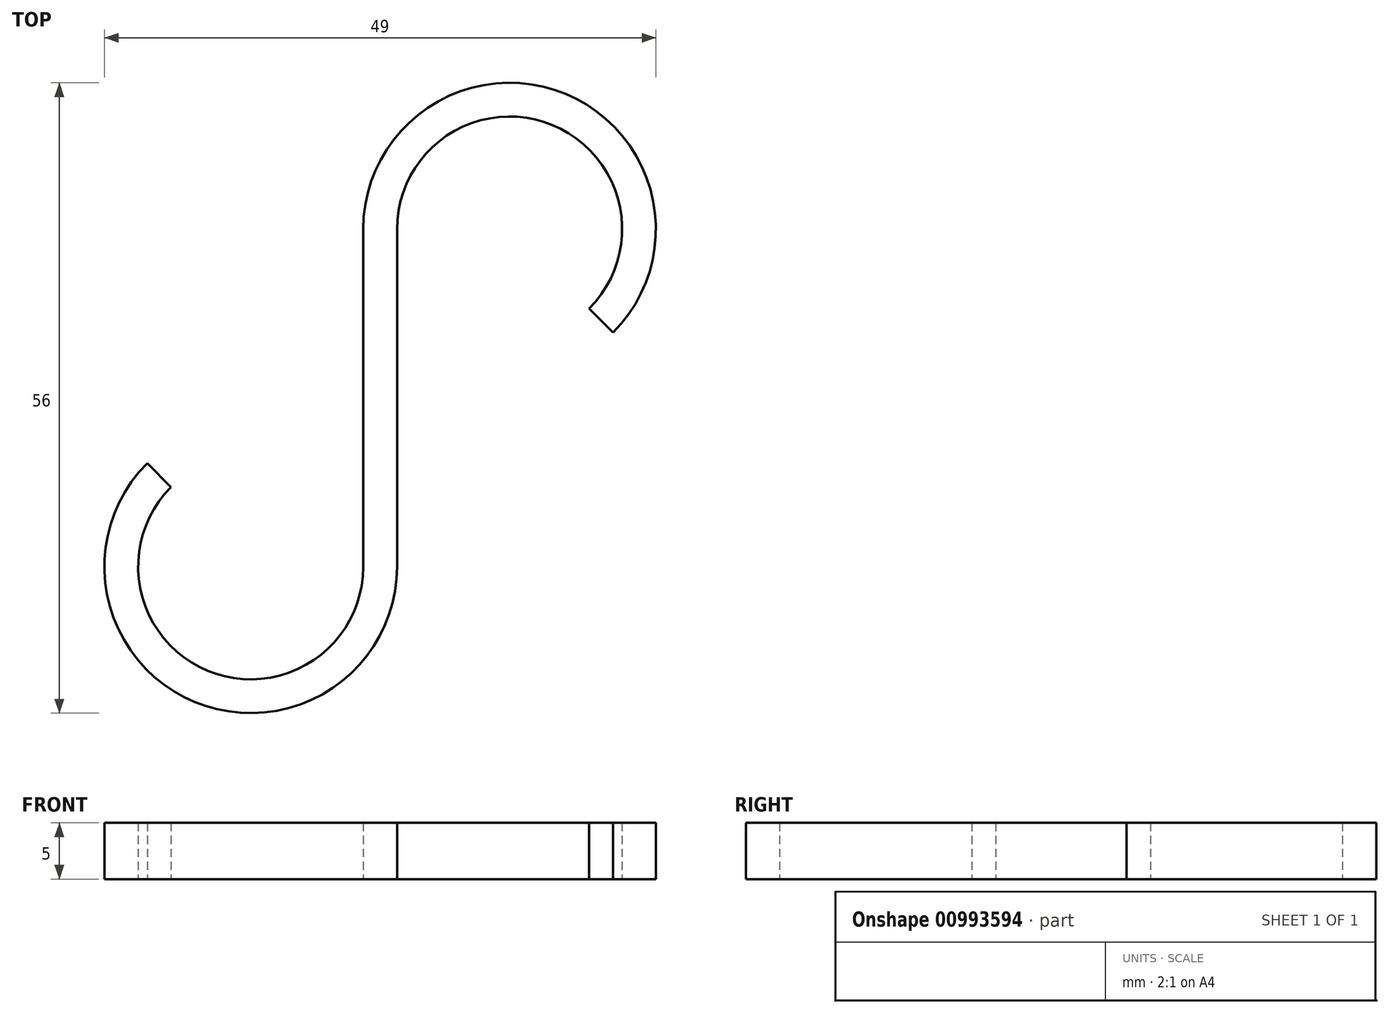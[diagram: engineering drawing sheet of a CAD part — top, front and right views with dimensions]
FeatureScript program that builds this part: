
annotation { "Feature Type Name" : "Feature", "Feature Type Description" : "" }
export const myFeature = defineFeature(function(context is Context, id is Id, definition is map)
    precondition{}
    {
        {
            var Q0;
            Q0=qCreatedBy(makeId("Top.planeOp"),FACE);
            var sketch = newSketch(context, id + "F0", { "sketchPlane" : qUnion([Q0])});
            skCircle(sketch, "E0", {"center": v(0, 0) * mm, "radius": 10 * mm});
            skCircle(sketch, "E1", {"center": v(0, 0) * mm, "radius": 13 * mm});
            skLineSegment(sketch, "E2", {"start": v(0, 0) * mm, "end": v(-10, 0) * mm});
            skLineSegment(sketch, "E3", {"start": v(0, -10) * mm, "end": v(10, -10) * mm});
            skLineSegment(sketch, "E4", {"start": v(10, -10) * mm, "end": v(10, 0) * mm});
            skLineSegment(sketch, "E5", {"start": v(0, 0) * mm, "end": v(10, -10) * mm});
            skLineSegment(sketch, "E6", {"start": v(-13, 0) * mm, "end": v(-13, -30) * mm});
            skLineSegment(sketch, "E7", {"start": v(-10, 0) * mm, "end": v(-10, -30) * mm});
            skLineSegment(sketch, "E8", {"start": v(-10, 0) * mm, "end": v(-13, 0) * mm});
            skLineSegment(sketch, "E9", {"start": v(-10, -30) * mm, "end": v(-13, -30) * mm});
            skLineSegment(sketch, "E10", {"start": v(-13, -30) * mm, "end": v(-23, -30) * mm});
            skCircle(sketch, "E11", {"center": v(-23, -30) * mm, "radius": 10 * mm});
            skCircle(sketch, "E12", {"center": v(-23, -30) * mm, "radius": 13 * mm});
            skLineSegment(sketch, "E13", {"start": v(-23, -30) * mm, "end": v(-23, -17) * mm});
            skLineSegment(sketch, "E14", {"start": v(-23, -30) * mm, "end": v(-36, -30) * mm});
            skLineSegment(sketch, "E15", {"start": v(-33, -30) * mm, "end": v(-33, -20) * mm});
            skLineSegment(sketch, "E16", {"start": v(-33, -20) * mm, "end": v(-23, -20) * mm});
            skLineSegment(sketch, "E17", {"start": v(-33, -20) * mm, "end": v(-23, -30) * mm});
            skSolve(sketch);
        }
        {
            var Q0;
            {var subQ1=sQuery(id+"F0.wireOp",EDGE,"E1");var subQ3=sQuery(id+"F0.wireOp",EDGE,"E7");var subQ4=makeQuery(id+"F0.imprint","INTERSECT",VERTEX,{"derivedFrom":[subQ1,subQ3]});Q0=makeQuery(id+"F0.imprint","IMPRINT",FACE,{"disambiguationData":[TD([[makeQuery(id+"F0.imprint","IMPRINT",EDGE,{"disambiguationData":[TD([[subQ4,1.0]])],"derivedFrom":subQ1}),-1.0]])]});}
            var Q1;
            {var subQ0=sQuery(id+"F0.wireOp",EDGE,"E8");Q1=makeQuery(id+"F0.imprint","IMPRINT",FACE,{"disambiguationData":[TD([[makeQuery(id+"F0.imprint","IMPRINT",EDGE,{"derivedFrom":subQ0}),1.0]])]});}
            var Q2;
            {var subQ0=sQuery(id+"F0.wireOp",EDGE,"E9");Q2=makeQuery(id+"F0.imprint","IMPRINT",FACE,{"disambiguationData":[TD([[makeQuery(id+"F0.imprint","IMPRINT",EDGE,{"derivedFrom":subQ0}),-1.0]])]});}
            var Q3;
            {var subQ0=sQuery(id+"F0.wireOp",EDGE,"E9");Q3=makeQuery(id+"F0.imprint","IMPRINT",FACE,{"disambiguationData":[TD([[makeQuery(id+"F0.imprint","IMPRINT",EDGE,{"derivedFrom":subQ0}),1.0]])]});}
            var Q4;
            {var subQ0=sQuery(id+"F0.wireOp",EDGE,"E8");Q4=makeQuery(id+"F0.imprint","IMPRINT",FACE,{"disambiguationData":[TD([[makeQuery(id+"F0.imprint","IMPRINT",EDGE,{"derivedFrom":subQ0}),-1.0]])]});}
            var Q5;
            {var subQ0=sQuery(id+"F0.wireOp",EDGE,"E14");var subQ1=sQuery(id+"F0.wireOp",EDGE,"E12");var subQ2=makeQuery(id+"F0.imprint","INTERSECT",VERTEX,{"derivedFrom":[subQ1,subQ0]});Q5=makeQuery(id+"F0.imprint","IMPRINT",FACE,{"disambiguationData":[TD([[makeQuery(id+"F0.imprint","IMPRINT",EDGE,{"disambiguationData":[TD([[subQ2,1.0]])],"derivedFrom":subQ1}),1.0]])]});}
            var Q6;
            {var subQ0=sQuery(id+"F0.wireOp",EDGE,"E15");var subQ5=sQuery(id+"F0.wireOp",EDGE,"E12");var subQ6=makeQuery(id+"F0.imprint","INTERSECT",VERTEX,{"derivedFrom":[subQ5,subQ0]});Q6=makeQuery(id+"F0.imprint","IMPRINT",FACE,{"disambiguationData":[TD([[makeQuery(id+"F0.imprint","IMPRINT",EDGE,{"disambiguationData":[TD([[subQ6,1.0]])],"derivedFrom":subQ5}),1.0]])]});}
            var Q7;
            {var subQ0=sQuery(id+"F0.wireOp",EDGE,"E4");var subQ1=sQuery(id+"F0.wireOp",EDGE,"E0");var subQ2=makeQuery(id+"F0.imprint","INTERSECT",VERTEX,{"derivedFrom":[subQ1,subQ0]});Q7=makeQuery(id+"F0.imprint","IMPRINT",FACE,{"disambiguationData":[TD([[makeQuery(id+"F0.imprint","IMPRINT",EDGE,{"disambiguationData":[TD([[subQ2,1.0]])],"derivedFrom":subQ1}),-1.0]])]});}
            extrude(context, id + "F1", {"entities" : qUnion([Q0, Q1, Q2, Q3, Q4, Q5, Q6, Q7]), "depth" : 5 * mm, "offsetDistance" : 25 * mm});
        }
    });
